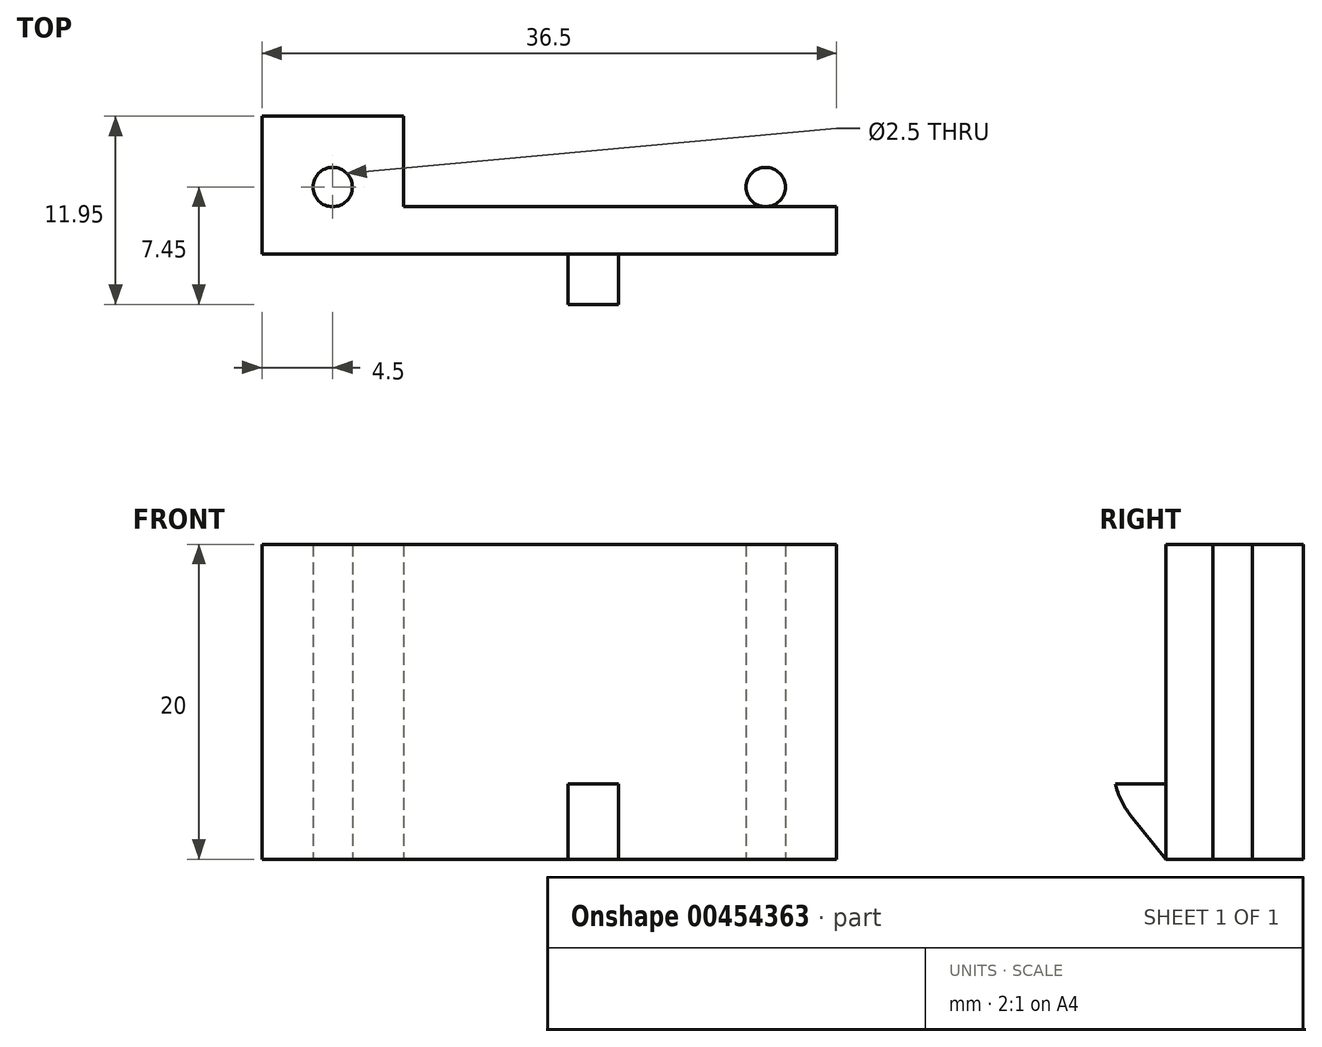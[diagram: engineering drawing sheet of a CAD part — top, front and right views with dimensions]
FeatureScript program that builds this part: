
annotation { "Feature Type Name" : "Feature", "Feature Type Description" : "" }
export const myFeature = defineFeature(function(context is Context, id is Id, definition is map)
    precondition{}
    {
        {
            var Q0;
            Q0=qCreatedBy(makeId("Top.planeOp"),FACE);
            var sketch = newSketch(context, id + "F0", { "sketchPlane" : qUnion([Q0])});
            skLineSegment(sketch, "E0", {"start": v(0, 0) * mm, "end": v(0, 11.01) * mm, "construction": true});
            skLineSegment(sketch, "E1", {"start": v(0, 0) * mm, "end": v(-12.5, 0) * mm, "construction": true});
            skCircle(sketch, "E2", {"center": v(-13.75, 0) * mm, "radius": 1.25 * mm});
            skLineSegment(sketch, "E3", {"start": v(-12.5, -1.46) * mm, "end": v(-12.5, 1.56) * mm, "construction": true});
            skLineSegment(sketch, "E4", {"start": v(-13.75, -1.25) * mm, "end": v(-13.75, -4.25) * mm, "construction": true});
            skLineSegment(sketch, "E5", {"start": v(-18.25, -1.25) * mm, "end": v(-9.25, -1.25) * mm});
            skPoint(sketch, "E6", {"position": v(-13.75, -4.25) * mm});
            skLineSegment(sketch, "E7", {"start": v(-13.75, 0) * mm, "end": v(-13.75, 4.5) * mm, "construction": true});
            skLineSegment(sketch, "E8", {"start": v(-18.25, -1.25) * mm, "end": v(-18.25, 4.5) * mm});
            skLineSegment(sketch, "E9", {"start": v(-18.25, 4.5) * mm, "end": v(-9.25, 4.5) * mm});
            skLineSegment(sketch, "E10", {"start": v(-9.25, -1.25) * mm, "end": v(-9.25, 4.5) * mm});
            skLineSegment(sketch, "E11", {"start": v(-18.25, -1.25) * mm, "end": v(-18.25, -4.25) * mm});
            skLineSegment(sketch, "E12", {"start": v(-18.25, -4.25) * mm, "end": v(0, -4.25) * mm});
            skLineSegment(sketch, "E13", {"start": v(-9.25, -1.25) * mm, "end": v(0, -1.25) * mm});
            skLineSegment(sketch, "E14.MirrorCS", {"start": v(0, 0) * mm, "end": v(12.5, 0) * mm, "construction": true});
            skPoint(sketch, "E15.MirrorP", {"position": v(13.75, -4.25) * mm});
            skLineSegment(sketch, "E16.MirrorCS", {"start": v(9.25, -1.25) * mm, "end": v(0, -1.25) * mm});
            skCircle(sketch, "E17.MirrorC", {"center": v(13.75, 0) * mm, "radius": 1.25 * mm});
            skLineSegment(sketch, "E18.MirrorCS", {"start": v(18.25, -4.25) * mm, "end": v(0, -4.25) * mm});
            skLineSegment(sketch, "E19.MirrorCS", {"start": v(18.25, -1.25) * mm, "end": v(18.25, -4.25) * mm});
            skLineSegment(sketch, "E20.MirrorCS", {"start": v(9.25, -1.25) * mm, "end": v(9.25, 4.5) * mm});
            skLineSegment(sketch, "E21.MirrorCS", {"start": v(18.25, 4.5) * mm, "end": v(9.25, 4.5) * mm});
            skLineSegment(sketch, "E22.MirrorCS", {"start": v(18.25, -1.25) * mm, "end": v(18.25, 4.5) * mm});
            skLineSegment(sketch, "E23.MirrorCS", {"start": v(13.75, -1.25) * mm, "end": v(13.75, -4.25) * mm, "construction": true});
            skLineSegment(sketch, "E24.MirrorCS", {"start": v(18.25, -1.25) * mm, "end": v(9.25, -1.25) * mm});
            skLineSegment(sketch, "E25.MirrorCS", {"start": v(12.5, -1.46) * mm, "end": v(12.5, 1.56) * mm, "construction": true});
            skLineSegment(sketch, "E26.MirrorCS", {"start": v(13.75, 0) * mm, "end": v(13.75, 4.5) * mm, "construction": true});
            skSolve(sketch);
        }
        {
            var Q0;
            Q0=makeQuery(id+"F0.imprint","IMPRINT",FACE,{"disambiguationData":[TD([[makeQuery(id+"F0.imprint","IMPRINT",EDGE,{"derivedFrom":sQuery(id+"F0.wireOp",EDGE,"E5")}),-1.0]])]});
            var Q1;
            Q1=makeQuery(id+"F0.imprint","IMPRINT",FACE,{"disambiguationData":[TD([[makeQuery(id+"F0.imprint","IMPRINT",EDGE,{"derivedFrom":sQuery(id+"F0.wireOp",EDGE,"E17.MirrorC")}),1.0]])]});
            var Q2;
            Q2=makeQuery(id+"F0.imprint","IMPRINT",FACE,{"disambiguationData":[TD([[makeQuery(id+"F0.imprint","IMPRINT",EDGE,{"derivedFrom":sQuery(id+"F0.wireOp",EDGE,"E2")}),-1.0]])]});
            extrude(context, id + "F1", {"entities" : qUnion([Q0, Q1, Q2]), "endBound" : BoundingType.SYMMETRIC, "depth" : 20 * mm});
        }
        {
            var Q0;
            Q0=makeQuery(id+"F1.opExtrude","SWEPT_FACE",FACE,{"disambiguationData":[OSD([sQuery(id+"F0.wireOp",EDGE,"E12"),sQuery(id+"F0.wireOp",EDGE,"E18.MirrorCS")])]});
            var sketch = newSketch(context, id + "F2", { "sketchPlane" : qUnion([Q0])});
            skLineSegment(sketch, "E27.bottom", {"start": v(4.4, 7) * mm, "end": v(-4.4, 7) * mm});
            skLineSegment(sketch, "E27.top", {"start": v(4.4, -7) * mm, "end": v(-4.4, -7) * mm});
            skLineSegment(sketch, "E27.left", {"start": v(4.4, 7) * mm, "end": v(4.4, -7) * mm});
            skLineSegment(sketch, "E27.right", {"start": v(-4.4, 7) * mm, "end": v(-4.4, -7) * mm});
            skPoint(sketch, "E27.middle", {"position": v(0, 0) * mm});
            skLineSegment(sketch, "E28.bottom", {"start": v(1.2, 7) * mm, "end": v(-1.2, 7) * mm});
            skLineSegment(sketch, "E28.top", {"start": v(1.2, -7) * mm, "end": v(-1.2, -7) * mm});
            skLineSegment(sketch, "E28.left", {"start": v(1.2, 7) * mm, "end": v(1.2, -7) * mm});
            skLineSegment(sketch, "E28.right", {"start": v(-1.2, 7) * mm, "end": v(-1.2, -7) * mm});
            skLineSegment(sketch, "E29", {"start": v(-4.4, -7) * mm, "end": v(-4.4, -5.2) * mm});
            skLineSegment(sketch, "E30", {"start": v(-4.4, -5.2) * mm, "end": v(4.4, -5.2) * mm});
            skSolve(sketch);
        }
        {
            var Q0;
            {var subQ0=sQuery(id+"F2.wireOp",EDGE,"E28.bottom");Q0=makeQuery(id+"F2.imprint","IMPRINT",FACE,{"disambiguationData":[TD([[makeQuery(id+"F2.imprint","IMPRINT",EDGE,{"derivedFrom":subQ0}),1.0]])]});}
            var Q1;
            {var subQ0=sQuery(id+"F2.wireOp",EDGE,"E29");Q1=makeQuery(id+"F2.imprint","IMPRINT",FACE,{"disambiguationData":[TD([[makeQuery(id+"F2.imprint","IMPRINT",EDGE,{"derivedFrom":subQ0}),-1.0]])]});}
            var Q2;
            {var subQ0=sQuery(id+"F2.wireOp",EDGE,"E28.top");Q2=makeQuery(id+"F2.imprint","IMPRINT",FACE,{"disambiguationData":[TD([[makeQuery(id+"F2.imprint","IMPRINT",EDGE,{"derivedFrom":subQ0}),-1.0]])]});}
            var Q3;
            {var subQ0=sQuery(id+"F2.wireOp",EDGE,"E27.left");var subQ1=sQuery(id+"F2.wireOp",EDGE,"E27.top");var subQ2=makeQuery(id+"F2.imprint","INTERSECT",VERTEX,{"derivedFrom":[subQ1,subQ0]});Q3=makeQuery(id+"F2.imprint","IMPRINT",FACE,{"disambiguationData":[TD([[makeQuery(id+"F2.imprint","IMPRINT",EDGE,{"disambiguationData":[TD([[subQ2,1.0]])],"derivedFrom":subQ0}),-1.0]])]});}
            extrude(context, id + "F3", {"entities" : qUnion([Q0, Q1, Q2, Q3]), "operationType" : NewBodyOperationType.ADD, "depth" : 2.7 * mm});
        }
        {
            var Q0;
            Q0=makeQuery(id+"F3.opExtrude","CAP_FACE",FACE,{"disambiguationData":[OSD([sQuery(id+"F2.wireOp",EDGE,"E27.top"),sQuery(id+"F2.wireOp",EDGE,"E27.left"),sQuery(id+"F2.wireOp",EDGE,"E28.bottom"),sQuery(id+"F2.wireOp",EDGE,"E28.top"),sQuery(id+"F2.wireOp",EDGE,"E28.left"),sQuery(id+"F2.wireOp",EDGE,"E28.right"),sQuery(id+"F2.wireOp",EDGE,"E29"),sQuery(id+"F2.wireOp",EDGE,"E30")])],"isStart":false});
            var sketch = newSketch(context, id + "F4", { "sketchPlane" : qUnion([Q0])});
            skLineSegment(sketch, "E31.bottom", {"start": v(-4.4, -7) * mm, "end": v(4.4, -7) * mm});
            skLineSegment(sketch, "E31.top", {"start": v(-4.4, 7) * mm, "end": v(4.4, 7) * mm});
            skLineSegment(sketch, "E31.left", {"start": v(-4.4, -7) * mm, "end": v(-4.4, 7) * mm});
            skLineSegment(sketch, "E31.right", {"start": v(4.4, -7) * mm, "end": v(4.4, 7) * mm});
            skSolve(sketch);
        }
        {
            var Q0;
            {var subQ1=sQuery(id+"F2.wireOp",EDGE,"E28.left");var subQ2=makeQuery(id+"F3.opExtrude","CAP_EDGE",EDGE,{"disambiguationData":[OSD([subQ1])],"isStart":false});Q0=makeQuery(id+"F4.imprint","IMPRINT",FACE,{"disambiguationData":[TD([[makeQuery(id+"F4.imprint","IMPRINT",EDGE,{"derivedFrom":subQ2}),1.0]])]});}
            var Q1;
            {var subQ1=sQuery(id+"F4.wireOp",EDGE,"E31.bottom");Q1=makeQuery(id+"F4.imprint","IMPRINT",FACE,{"disambiguationData":[TD([[makeQuery(id+"F4.imprint","IMPRINT",EDGE,{"derivedFrom":subQ1}),-1.0]])]});}
            var Q2;
            {var subQ1=sQuery(id+"F2.wireOp",EDGE,"E28.right");var subQ2=makeQuery(id+"F3.opExtrude","CAP_EDGE",EDGE,{"disambiguationData":[OSD([subQ1])],"isStart":false});Q2=makeQuery(id+"F4.imprint","IMPRINT",FACE,{"disambiguationData":[TD([[makeQuery(id+"F4.imprint","IMPRINT",EDGE,{"derivedFrom":subQ2}),-1.0]])]});}
            extrude(context, id + "F5", {"entities" : qUnion([Q0, Q1, Q2]), "operationType" : NewBodyOperationType.ADD, "depth" : .5 * mm});
        }
        {
            var Q0;
            Q0=makeQuery(id+"F5.boolean.opBoolean","MERGE",FACE,{"derivedFrom":[makeQuery(id+"F3.opExtrude","SWEPT_FACE",FACE,{"disambiguationData":[OSD([sQuery(id+"F2.wireOp",EDGE,"E27.top"),sQuery(id+"F2.wireOp",EDGE,"E28.top")])]}),makeQuery(id+"F5.opExtrude","SWEPT_FACE",FACE,{"disambiguationData":[OSD([sQuery(id+"F4.wireOp",EDGE,"E31.bottom")])]})]});
            var Q1;
            Q1=makeQuery(id+"F1.opExtrude","CAP_FACE",FACE,{"disambiguationData":[OSD([sQuery(id+"F0.wireOp",EDGE,"E2"),sQuery(id+"F0.wireOp",EDGE,"E8"),sQuery(id+"F0.wireOp",EDGE,"E9"),sQuery(id+"F0.wireOp",EDGE,"E10"),sQuery(id+"F0.wireOp",EDGE,"E11"),sQuery(id+"F0.wireOp",EDGE,"E12"),sQuery(id+"F0.wireOp",EDGE,"E13"),sQuery(id+"F0.wireOp",EDGE,"E16.MirrorCS"),sQuery(id+"F0.wireOp",EDGE,"E17.MirrorC"),sQuery(id+"F0.wireOp",EDGE,"E18.MirrorCS"),sQuery(id+"F0.wireOp",EDGE,"E19.MirrorCS"),sQuery(id+"F0.wireOp",EDGE,"E20.MirrorCS"),sQuery(id+"F0.wireOp",EDGE,"E21.MirrorCS"),sQuery(id+"F0.wireOp",EDGE,"E22.MirrorCS")])],"isStart":true});
            extrude(context, id + "F6", {"entities" : qUnion([Q0]), "operationType" : NewBodyOperationType.ADD, "endBound" : BoundingType.UP_TO_SURFACE, "endBoundEntityFace" : qUnion([Q1]), "depth" : 25 * mm});
        }
        {
            var Q0;
            Q0=makeQuery(id+"F6.opExtrude","CAP_EDGE",EDGE,{"disambiguationData":[OSD([sQuery(id+"F4.wireOp",EDGE,"E31.bottom")])],"isStart":false});
            chamfer(context, id + "F7", {"entities" : qUnion([Q0]), "chamferType" : ChamferType.TWO_OFFSETS, "width1" : 4 * mm, "oppositeDirection" : false, "width2" : 3.2 * mm, "tangentPropagation" : true});
        }
        {
            var Q0;
            {var subQ0=sQuery(id+"F4.wireOp",EDGE,"E31.bottom");Q0=makeQuery(id+"F7.opChamfer","BLEND_EDGE",EDGE,{"blendedFrom":[makeQuery(id+"F6.opExtrude","CAP_EDGE",EDGE,{"disambiguationData":[OSD([subQ0])],"isStart":false}),makeQuery(id+"F6.boolean.opBoolean","MERGE",FACE,{"derivedFrom":[makeQuery(id+"F5.opExtrude","CAP_FACE",FACE,{"disambiguationData":[OSD([subQ0,sQuery(id+"F4.wireOp",EDGE,"E31.top"),sQuery(id+"F4.wireOp",EDGE,"E31.left"),sQuery(id+"F4.wireOp",EDGE,"E31.right")])],"isStart":false}),makeQuery(id+"F6.opExtrude","SWEPT_FACE",FACE,{"disambiguationData":[OSD([subQ0])]})]})],"blendedInto":[makeQuery(id+"F6.boolean.opBoolean","MERGE",FACE,{"derivedFrom":[makeQuery(id+"F5.opExtrude","CAP_FACE",FACE,{"disambiguationData":[OSD([subQ0,sQuery(id+"F4.wireOp",EDGE,"E31.top"),sQuery(id+"F4.wireOp",EDGE,"E31.left"),sQuery(id+"F4.wireOp",EDGE,"E31.right")])],"isStart":false}),makeQuery(id+"F6.opExtrude","SWEPT_FACE",FACE,{"disambiguationData":[OSD([subQ0])]})]})]});}
            fillet(context, id + "F8", {"entities" : qUnion([Q0]), "radius" : 5 * mm, "tangentPropagation" : true, "allowEdgeOverflow" : false});
        }
    });
